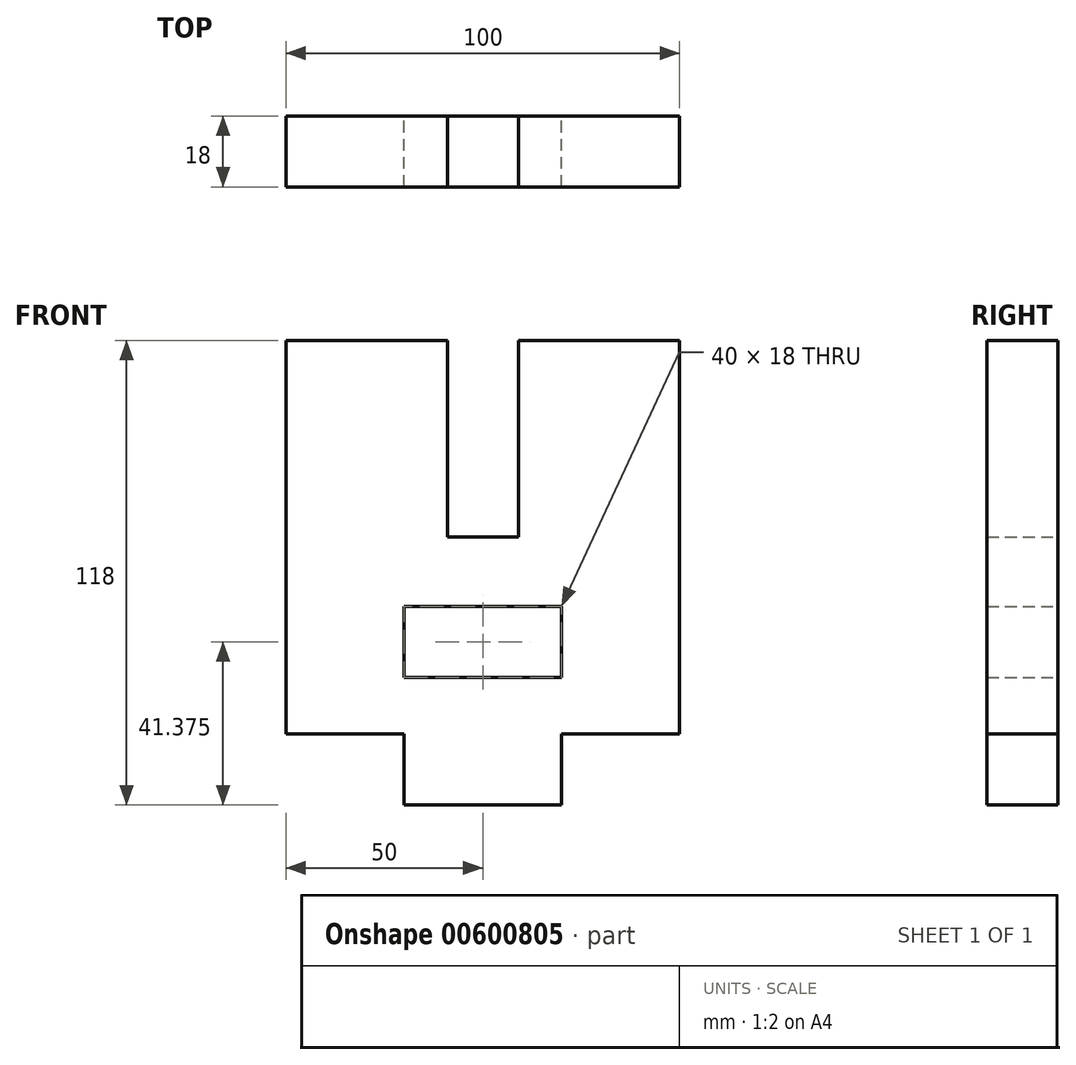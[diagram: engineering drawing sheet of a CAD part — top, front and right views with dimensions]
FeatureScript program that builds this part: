
annotation { "Feature Type Name" : "Feature", "Feature Type Description" : "" }
export const myFeature = defineFeature(function(context is Context, id is Id, definition is map)
    precondition{}
    {
        {
            var Q0;
            Q0=qCreatedBy(makeId("Front.planeOp"),FACE);
            var sketch = newSketch(context, id + "F0", { "sketchPlane" : qUnion([Q0])});
            skLineSegment(sketch, "E0.top", {"start": v(50, 50) * mm, "end": v(9, 50) * mm});
            skLineSegment(sketch, "E0.left", {"start": v(50, -50) * mm, "end": v(50, 50) * mm});
            skLineSegment(sketch, "E0.right", {"start": v(-50, -50) * mm, "end": v(-50, 50) * mm});
            skPoint(sketch, "E0.middle", {"position": v(0, 0) * mm});
            skLineSegment(sketch, "E1.bottom", {"start": v(9, 0) * mm, "end": v(-9, 0) * mm});
            skLineSegment(sketch, "E1.left", {"start": v(9, 0) * mm, "end": v(9, 50) * mm});
            skLineSegment(sketch, "E1.right", {"start": v(-9, 0) * mm, "end": v(-9, 50) * mm});
            skLineSegment(sketch, "E2.trimOffspring", {"start": v(-9, 50) * mm, "end": v(-50, 50) * mm});
            skLineSegment(sketch, "E3.bottom", {"start": v(20, -68) * mm, "end": v(-20, -68) * mm});
            skLineSegment(sketch, "E3.left", {"start": v(20, -68) * mm, "end": v(20, -50) * mm});
            skLineSegment(sketch, "E3.right", {"start": v(-20, -68) * mm, "end": v(-20, -50) * mm});
            skLineSegment(sketch, "E4", {"start": v(-50, -50) * mm, "end": v(-20, -50) * mm});
            skLineSegment(sketch, "E5.trimOffspring", {"start": v(20, -50) * mm, "end": v(50, -50) * mm});
            skLineSegment(sketch, "E6.bottom", {"start": v(20, -35.63) * mm, "end": v(-20, -35.63) * mm});
            skLineSegment(sketch, "E6.top", {"start": v(20, -17.63) * mm, "end": v(-20, -17.63) * mm});
            skLineSegment(sketch, "E6.left", {"start": v(20, -35.63) * mm, "end": v(20, -17.63) * mm});
            skLineSegment(sketch, "E6.right", {"start": v(-20, -35.63) * mm, "end": v(-20, -17.63) * mm});
            skPoint(sketch, "E6.middle", {"position": v(0, -26.63) * mm});
            skSolve(sketch);
        }
        {
            var Q0;
            Q0=makeQuery(id+"F0.imprint","IMPRINT",FACE,{"disambiguationData":[TD([[makeQuery(id+"F0.imprint","IMPRINT",EDGE,{"derivedFrom":sQuery(id+"F0.wireOp",EDGE,"E0.top")}),1.0]])]});
            extrude(context, id + "F1", {"entities" : qUnion([Q0]), "depth" : 18 * mm, "offsetDistance" : 25 * mm});
        }
    });
